# Revit family: Podajnik_reczników_ZZ HIT S
name_source: partatom
category: Furniture
units: mm (PartAtom-declared; Revit-internal decimal feet)

## family parameters
Always vertical = Yes
Cut with Voids When Loaded = No
Host = Wall
Room Calculation Point = No
Shared = No

## types (1)
- Type 1
    Depth / Glebokosc = 120 mm  [stored 0.393701 ft]
    Description = Podajnik ręczników ZZ HIT S to naścienny, zamykany na kluczyk, stalowy model o uniwersalnym wyglądzie. Matowe wykończenie oraz niewielkie rozmiary sprawiają, że cieszy się on dużym powodzeniem i ma zastosowanie w różnych obiektach użyteczności publicznej o średnim natężeniu ruchu. Dzięki wizjerowi w kształcie litery „S” możliwa jest wygodna kontrola poziomu papieru wewnątrz. Dozownik ręczników HIT jest bardzo trwałym i solidnym pojemnikiem, który z powodzeniem może spełniać swoją rolę przez lata.
    Height / Wysokosc = 210 mm
    Manufacturer = FANECO.com
    Manufacturer code / Kod producenta = 5901764292531
    Material = Stal nierdzewna szczotkowana
    Material finish / Wykonczenie = Stal nierdzewna szczotkowana, mat.
    Model = HIT S
    Product code / Kod produktu = P300SJB
    URL = https://faneco.com
    Weight / Waga = 1.5 kg
    Width / Szerokosc = 270 mm

note: [stored X ft] marks values corroborated as IEEE doubles in the binary element streams (Revit-internal decimal feet)

## geometry (parser evidence)
native form markers: Blend x8, Sweep x7
no freeform markers — native parametric forms only
